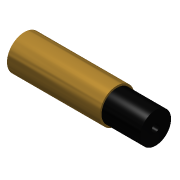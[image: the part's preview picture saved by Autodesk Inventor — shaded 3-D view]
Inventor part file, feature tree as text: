
AUTODESK INVENTOR PART (.ipt)
format: ipt  version: 2016 (Build 200138000, 138)  size: 92,672 bytes
history: native  units: in
note: dims shown in document units (in); Inventor stores cm internally (conversion verified against a paired STEP export)
features: extrude x3, sketch x3
ambient origin geometry x8: Origin, YZ Plane, XZ Plane, XY Plane, X Axis, Y Axis, Z Axis, Center Point
bodies: Solid1 (feature_tree)
feature tree (6):
  extrude  "Extrusion1"  Depth=3.0in TaperAngle=0.0deg
  extrude  "Extrusion2"  Depth=1.25in TaperAngle=0.0deg
  extrude  "Extrusion3"  Depth=0.4in TaperAngle=0.0deg
  sketch  "Sketch1"  dims[d0=1.125in d1=3.0in d2=0.0in]
  sketch  "Sketch2"  dims[d3=1.0in d4=1.25in d5=0.0in]
  sketch  "Sketch3"  dims[d6=0.25in d7=0.4in d8=0.0in]
